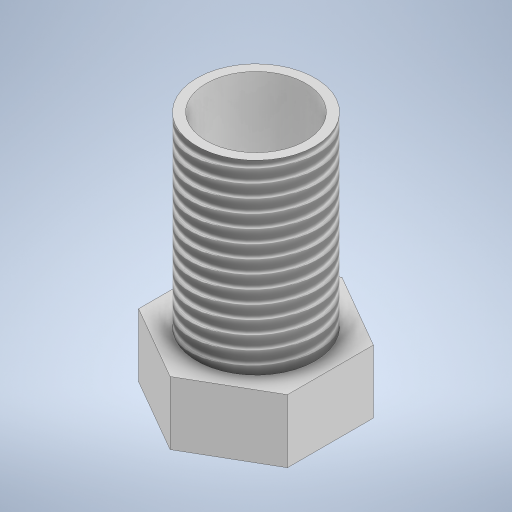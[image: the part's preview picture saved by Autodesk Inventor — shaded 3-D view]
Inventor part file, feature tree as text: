
AUTODESK INVENTOR PART (.ipt)
format: ipt  version: 2023 (Build 270158000, 158)  size: 290,304 bytes
history: native  units: in
note: dims shown in document units (in); Inventor stores cm internally (conversion verified against a paired STEP export)
features: sketch x2, revolve x1, shell x1, thread x1, extrude x1
ambient origin geometry x8: Origin, YZ Plane, XZ Plane, XY Plane, X Axis, Y Axis, Z Axis, Center Point
bodies: Solid1 (feature_tree)
feature tree (6):
  revolve  "Revolution1"  [1 undecoded]
  shell  "Shell1"  Thickness=90.0deg
  thread  "Thread1"  [1 undecoded]
  extrude  "Extrusion1"  Depth=0.315in
  sketch  "Sketch1"  dims[d0=0.125in d1=0.3937in d2=90.0deg d3=0.0197in]
  sketch  "Sketch2"  dims[d4=0.3937in d5=0.0in d6=0.315in d7=0.1339in d8=0.0in]
note: 2 required parameter values undecoded (feature->parameter linkage not recoverable at this tier; creation-order binding heuristic only, values carry confidence <= 0.55)